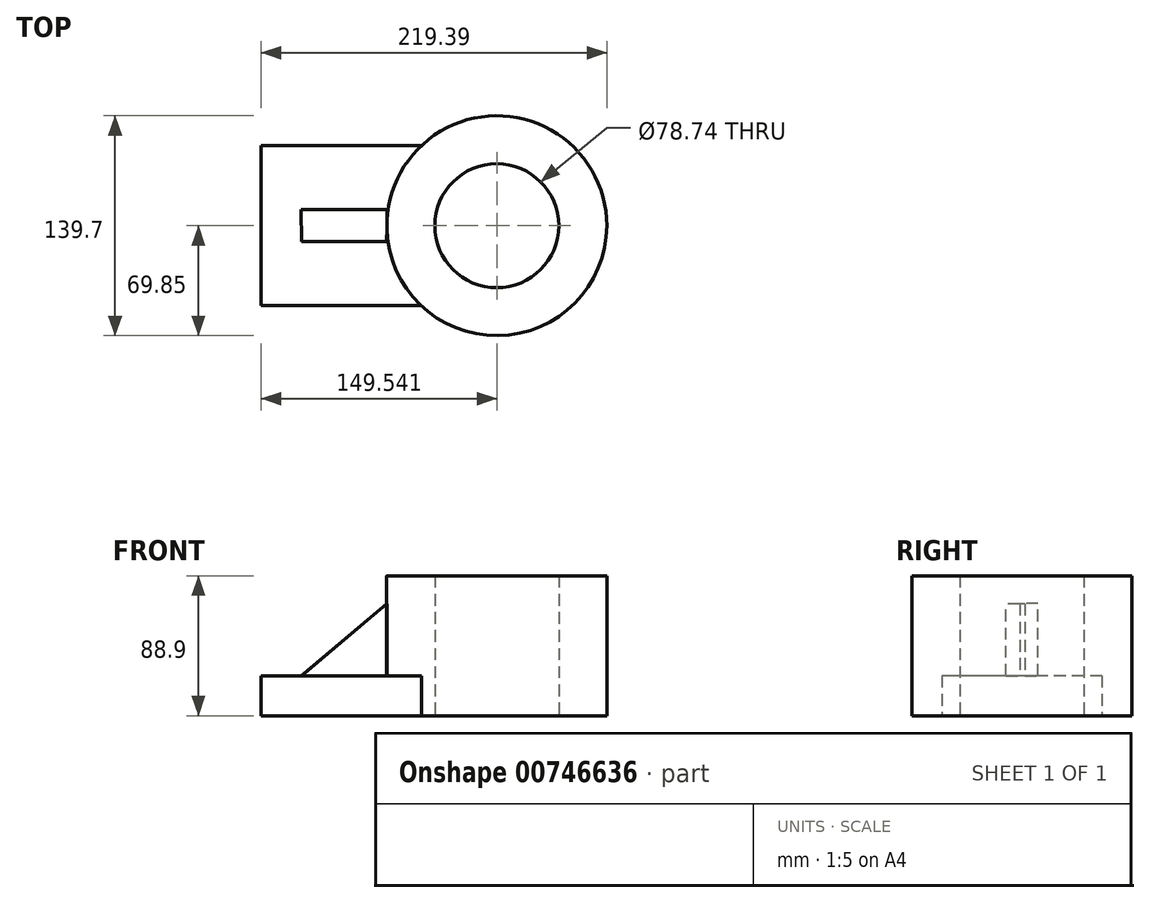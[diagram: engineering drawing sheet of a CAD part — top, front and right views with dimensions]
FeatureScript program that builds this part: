
annotation { "Feature Type Name" : "Feature", "Feature Type Description" : "" }
export const myFeature = defineFeature(function(context is Context, id is Id, definition is map)
    precondition{}
    {
        {
            var Q0;
            Q0=qCreatedBy(makeId("Top.planeOp"),FACE);
            var sketch = newSketch(context, id + "F0", { "sketchPlane" : qUnion([Q0])});
            skLineSegment(sketch, "E0.bottom", {"start": v(-50.8, 50.8) * mm, "end": v(50.8, 50.8) * mm});
            skLineSegment(sketch, "E0.top", {"start": v(-50.8, -50.8) * mm, "end": v(50.8, -50.8) * mm});
            skLineSegment(sketch, "E0.left", {"start": v(-50.8, 50.8) * mm, "end": v(-50.8, -50.8) * mm});
            skCircle(sketch, "E1", {"center": v(98.74, 0) * mm, "radius": 69.85 * mm});
            skCircle(sketch, "E2", {"center": v(98.74, 0) * mm, "radius": 39.37 * mm});
            skSolve(sketch);
        }
        {
            var Q0;
            Q0=makeQuery(id+"F0.imprint","IMPRINT",FACE,{"disambiguationData":[TD([[makeQuery(id+"F0.imprint","IMPRINT",EDGE,{"derivedFrom":sQuery(id+"F0.wireOp",EDGE,"E2")}),-1.0]])]});
            extrude(context, id + "F1", {"entities" : qUnion([Q0]), "depth" : 88.9 * mm, "offsetDistance" : 25.4 * mm});
        }
        {
            var Q0;
            {var subQ0=sQuery(id+"F0.wireOp",EDGE,"E0.bottom");Q0=makeQuery(id+"F0.imprint","IMPRINT",FACE,{"disambiguationData":[TD([[makeQuery(id+"F0.imprint","IMPRINT",EDGE,{"derivedFrom":subQ0}),-1.0]])]});}
            extrude(context, id + "F2", {"entities" : qUnion([Q0]), "operationType" : NewBodyOperationType.ADD, "depth" : 25.4 * mm, "offsetDistance" : 25.4 * mm});
        }
        {
            var Q0;
            Q0=qCreatedBy(makeId("Front.planeOp"),FACE);
            cPlane(context, id + "F3", {"entities" : qUnion([Q0]), "cplaneType" : CPlaneType.OFFSET, "offset" : 10.16 * mm, "width" : 152.4 * mm, "height" : 152.4 * mm});
        }
        {
            var Q0;
            Q0=qCreatedBy(id+"F3.planeOp",FACE);
            var sketch = newSketch(context, id + "F4", { "sketchPlane" : qUnion([Q0])});
            skLineSegment(sketch, "E3", {"start": v(28.9, 71.12) * mm, "end": v(28.9, 25.4) * mm});
            skLineSegment(sketch, "E4", {"start": v(28.9, 25.4) * mm, "end": v(-25.4, 25.4) * mm});
            skLineSegment(sketch, "E5", {"start": v(-25.4, 25.4) * mm, "end": v(28.9, 71.12) * mm});
            skSolve(sketch);
        }
        {
            var Q0;
            Q0=makeQuery(id+"F4.imprint","IMPRINT",FACE,{"disambiguationData":[TD([[makeQuery(id+"F4.imprint","IMPRINT",EDGE,{"derivedFrom":sQuery(id+"F4.wireOp",EDGE,"E3")}),-1.0]])]});
            extrude(context, id + "F5", {"entities" : qUnion([Q0]), "operationType" : NewBodyOperationType.ADD, "oppositeDirection" : true, "depth" : 20.32 * mm, "offsetDistance" : 25.4 * mm, "hasDraft" : true, "draftAngle" : 0.1 * degree});
        }
    });
